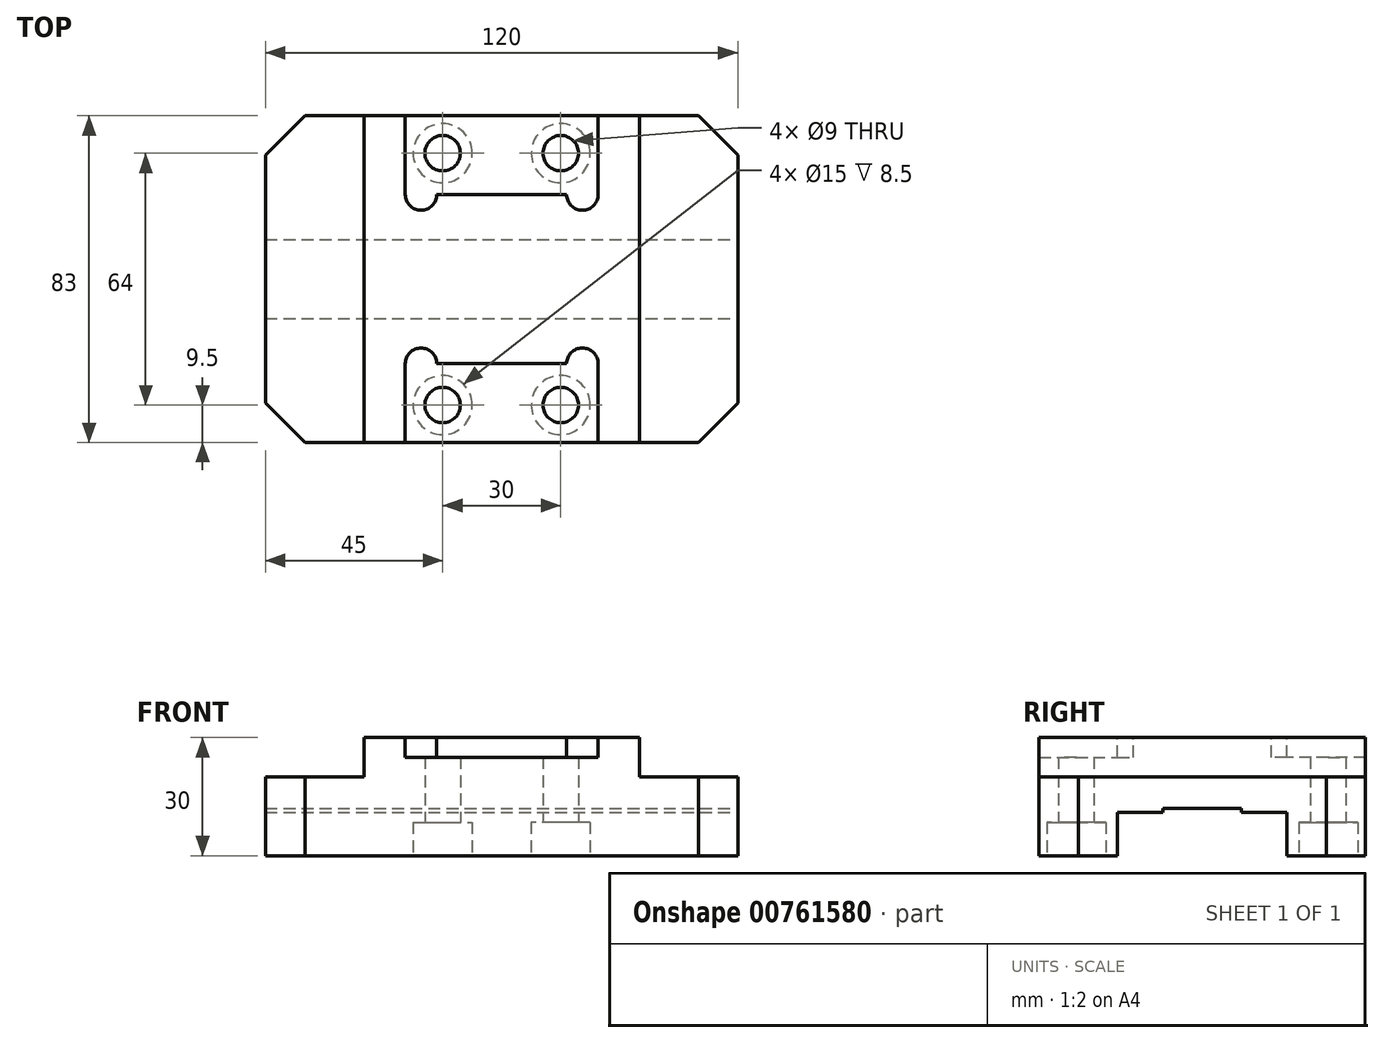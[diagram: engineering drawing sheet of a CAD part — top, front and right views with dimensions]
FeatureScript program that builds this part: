
annotation { "Feature Type Name" : "Feature", "Feature Type Description" : "" }
export const myFeature = defineFeature(function(context is Context, id is Id, definition is map)
    precondition{}
    {
        {
            var Q0;
            Q0=qCreatedBy(makeId("Top.planeOp"),FACE);
            var sketch = newSketch(context, id + "F0", { "sketchPlane" : qUnion([Q0])});
            skLineSegment(sketch, "E0.bottom", {"start": v(0, 0) * mm, "end": v(-60, 0) * mm});
            skLineSegment(sketch, "E0.top", {"start": v(0, -41.5) * mm, "end": v(-60, -41.5) * mm});
            skLineSegment(sketch, "E0.left", {"start": v(0, 0) * mm, "end": v(0, -41.5) * mm});
            skLineSegment(sketch, "E0.right", {"start": v(-60, 0) * mm, "end": v(-60, -41.5) * mm});
            skLineSegment(sketch, "E1", {"start": v(-35, 0) * mm, "end": v(-35, -41.5) * mm});
            skLineSegment(sketch, "E2", {"start": v(-24.5, -41.5) * mm, "end": v(-24.5, -21.5) * mm});
            skArc(sketch, "E3", {"start": v(-16.5, -21.5) * mm, "mid": v(-20.5, -17.5) * mm, "end": v(-24.5, -21.5) * mm});
            skLineSegment(sketch, "E4", {"start": v(-16.5, -21.5) * mm, "end": v(0, -21.5) * mm});
            skSolve(sketch);
        }
        {
            var Q0;
            Q0=makeQuery(id+"F0.imprint","IMPRINT",FACE,{"disambiguationData":[TD([[makeQuery(id+"F0.imprint","IMPRINT",EDGE,{"derivedFrom":sQuery(id+"F0.wireOp",EDGE,"E0.bottom")}),1.0]])]});
            var Q1;
            {var subQ0=sQuery(id+"F0.wireOp",EDGE,"E1");Q1=makeQuery(id+"F0.imprint","IMPRINT",FACE,{"disambiguationData":[TD([[makeQuery(id+"F0.imprint","IMPRINT",EDGE,{"derivedFrom":subQ0}),1.0]])]});}
            var Q2;
            {var subQ0=sQuery(id+"F0.wireOp",EDGE,"E2");Q2=makeQuery(id+"F0.imprint","IMPRINT",FACE,{"disambiguationData":[TD([[makeQuery(id+"F0.imprint","IMPRINT",EDGE,{"derivedFrom":subQ0}),-1.0]])]});}
            extrude(context, id + "F1", {"entities" : qUnion([Q0, Q1, Q2]), "depth" : 30 * mm, "offsetDistance" : 25 * mm});
        }
        {
            var Q0;
            Q0=makeQuery(id+"F1.opExtrude","CAP_FACE",FACE,{"disambiguationData":[OSD([sQuery(id+"F0.wireOp",EDGE,"E0.bottom"),sQuery(id+"F0.wireOp",EDGE,"E0.top"),sQuery(id+"F0.wireOp",EDGE,"E0.left"),sQuery(id+"F0.wireOp",EDGE,"E0.right")])],"isStart":false});
            var sketch = newSketch(context, id + "F2", { "sketchPlane" : qUnion([Q0])});
            skLineSegment(sketch, "E5.0", {"start": v(-35, 0) * mm, "end": v(-35, -41.5) * mm});
            skLineSegment(sketch, "E6.2", {"start": v(0, -41.5) * mm, "end": v(-60, -41.5) * mm});
            skLineSegment(sketch, "E7.0", {"start": v(0, 0) * mm, "end": v(-60, 0) * mm});
            skLineSegment(sketch, "E8.0", {"start": v(-60, 0) * mm, "end": v(-60, -41.5) * mm});
            skSolve(sketch);
        }
        {
            var Q0;
            {var subQ0=sQuery(id+"F2.wireOp",EDGE,"E5.0");Q0=makeQuery(id+"F2.imprint","IMPRINT",FACE,{"disambiguationData":[TD([[makeQuery(id+"F2.imprint","IMPRINT",EDGE,{"derivedFrom":subQ0}),-1.0]])]});}
            extrude(context, id + "F3", {"entities" : qUnion([Q0]), "operationType" : NewBodyOperationType.REMOVE, "oppositeDirection" : true, "depth" : 10 * mm, "offsetDistance" : 25 * mm});
        }
        {
            var Q0;
            Q0=makeQuery(id+"F1.opExtrude","SWEPT_EDGE",EDGE,{"disambiguationData":[OSD([sQuery(id+"F0.wireOp",EDGE,"E0.top"),sQuery(id+"F0.wireOp",EDGE,"E0.right")])]});
            chamfer(context, id + "F4", {"entities" : qUnion([Q0]), "width" : 10 * mm, "tangentPropagation" : true});
        }
        {
            var Q0;
            Q0=makeQuery(id+"F1.opExtrude","CAP_FACE",FACE,{"disambiguationData":[OSD([sQuery(id+"F0.wireOp",EDGE,"E0.bottom"),sQuery(id+"F0.wireOp",EDGE,"E0.top"),sQuery(id+"F0.wireOp",EDGE,"E0.left"),sQuery(id+"F0.wireOp",EDGE,"E0.right")])],"isStart":false});
            var sketch = newSketch(context, id + "F5", { "sketchPlane" : qUnion([Q0])});
            skArc(sketch, "E9.0", {"start": v(-16.5, -21.5) * mm, "mid": v(-20.5, -17.5) * mm, "end": v(-24.5, -21.5) * mm});
            skLineSegment(sketch, "E9.1", {"start": v(-16.5, -21.5) * mm, "end": v(0, -21.5) * mm});
            skLineSegment(sketch, "E9.2", {"start": v(0, 0) * mm, "end": v(0, -41.5) * mm});
            skLineSegment(sketch, "E9.3", {"start": v(-24.5, -41.5) * mm, "end": v(-24.5, -21.5) * mm});
            skLineSegment(sketch, "E9.4", {"start": v(0, -41.5) * mm, "end": v(-60, -41.5) * mm});
            skSolve(sketch);
        }
        {
            var Q0;
            Q0=makeQuery(id+"F5.imprint","IMPRINT",FACE,{"disambiguationData":[TD([[makeQuery(id+"F5.imprint","IMPRINT",EDGE,{"derivedFrom":sQuery(id+"F5.wireOp",EDGE,"E9.0")}),1.0]])]});
            extrude(context, id + "F6", {"entities" : qUnion([Q0]), "operationType" : NewBodyOperationType.REMOVE, "oppositeDirection" : true, "depth" : 5 * mm, "offsetDistance" : 25 * mm});
        }
        {
            var Q0;
            Q0=qCreatedBy(makeId("Right.planeOp"),FACE);
            var sketch = newSketch(context, id + "F7", { "sketchPlane" : qUnion([Q0])});
            skLineSegment(sketch, "E10", {"start": v(0, 12) * mm, "end": v(-10, 12) * mm});
            skLineSegment(sketch, "E11", {"start": v(-10, 12) * mm, "end": v(-10, 11) * mm});
            skLineSegment(sketch, "E12", {"start": v(-10, 11) * mm, "end": v(-21.5, 11) * mm});
            skLineSegment(sketch, "E13", {"start": v(-21.5, 11) * mm, "end": v(-21.5, 0) * mm});
            skLineSegment(sketch, "E14", {"start": v(-21.5, 0) * mm, "end": v(0, 0) * mm});
            skLineSegment(sketch, "E15", {"start": v(0, 0) * mm, "end": v(0, 12) * mm});
            skSolve(sketch);
        }
        {
            var Q0;
            Q0=makeQuery(id+"F7.imprint","IMPRINT",FACE,{"disambiguationData":[TD([[makeQuery(id+"F7.imprint","IMPRINT",EDGE,{"derivedFrom":sQuery(id+"F7.wireOp",EDGE,"E10")}),1.0]])]});
            extrude(context, id + "F8", {"entities" : qUnion([Q0]), "operationType" : NewBodyOperationType.REMOVE, "endBound" : BoundingType.THROUGH_ALL, "oppositeDirection" : true, "depth" : 25 * mm, "offsetDistance" : 25 * mm});
        }
        {
            var Q0;
            Q0=qCreatedBy(makeId("Top.planeOp"),FACE);
            var sketch = newSketch(context, id + "F9", { "sketchPlane" : qUnion([Q0])});
            skPoint(sketch, "E16", {"position": v(-15, -32) * mm});
            skSolve(sketch);
        }
        {
            var Q0;
            Q0=sQuery(id+"F9.wireOp",VERTEX,"E16");
            var Q1;
            Q1=makeQuery(id+"F1.opExtrude","SWEPT_BODY",BODY,{"disambiguationData":[OSD([sQuery(id+"F0.wireOp",EDGE,"E0.bottom"),sQuery(id+"F0.wireOp",EDGE,"E0.top"),sQuery(id+"F0.wireOp",EDGE,"E0.left"),sQuery(id+"F0.wireOp",EDGE,"E0.right")])]});
            hole(context, id + "F10", {"style" : HoleStyle.C_BORE, "endStyle" : HoleEndStyle.THROUGH, "oppositeDirection" : true, "holeDiameter" : 9 * mm, "cBoreDiameter" : 15 * mm, "cBoreDepth" : 8.5 * mm, "majorDiameter" : 5 * mm, "isTappedThrough" : true, "tappedDepth" : 12 * mm, "tapClearance" : 6, "startFromSketch" : true, "locations" : qUnion([Q0]), "scope" : qUnion([Q1])});
        }
        {
            var Q0;
            Q0=makeQuery(id+"F1.opExtrude","SWEPT_BODY",BODY,{"disambiguationData":[OSD([sQuery(id+"F0.wireOp",EDGE,"E0.bottom"),sQuery(id+"F0.wireOp",EDGE,"E0.top"),sQuery(id+"F0.wireOp",EDGE,"E0.left"),sQuery(id+"F0.wireOp",EDGE,"E0.right")])]});
            var Q1;
            Q1=qCreatedBy(makeId("Right.planeOp"),FACE);
            mirror(context, id + "F11", {"operationType" : NewBodyOperationType.ADD, "entities" : qUnion([Q0]), "mirrorPlane" : qUnion([Q1])});
        }
        {
            var Q0;
            Q0=makeQuery(id+"F1.opExtrude","SWEPT_BODY",BODY,{"disambiguationData":[OSD([sQuery(id+"F0.wireOp",EDGE,"E0.bottom"),sQuery(id+"F0.wireOp",EDGE,"E0.top"),sQuery(id+"F0.wireOp",EDGE,"E0.left"),sQuery(id+"F0.wireOp",EDGE,"E0.right")])]});
            var Q1;
            Q1=qCreatedBy(makeId("Front.planeOp"),FACE);
            mirror(context, id + "F12", {"operationType" : NewBodyOperationType.ADD, "entities" : qUnion([Q0]), "mirrorPlane" : qUnion([Q1])});
        }
    });
